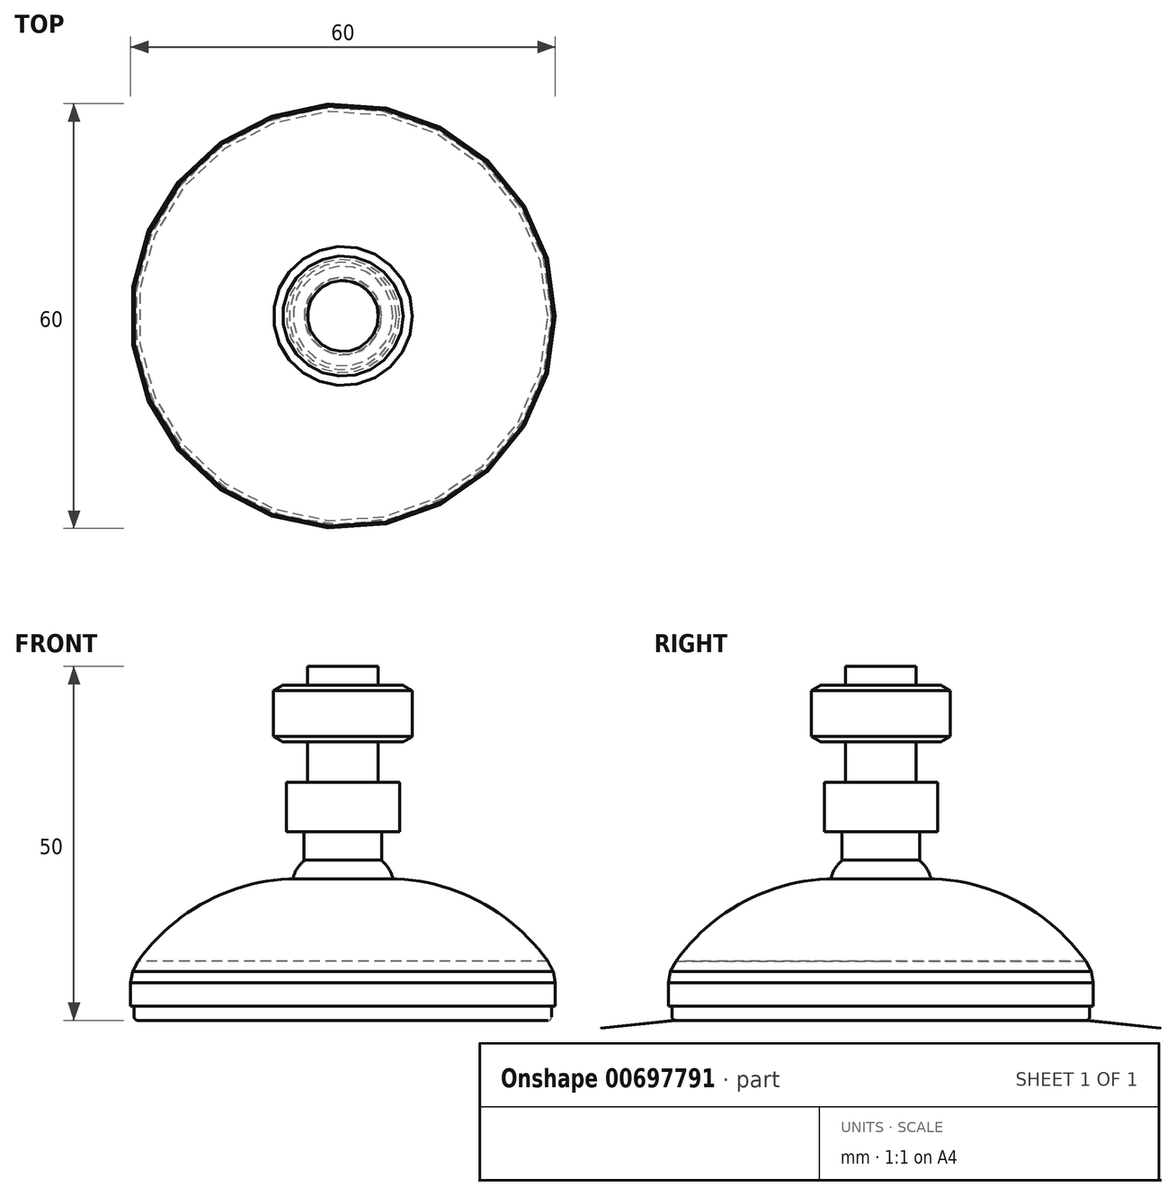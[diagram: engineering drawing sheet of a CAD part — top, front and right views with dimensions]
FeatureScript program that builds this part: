
annotation { "Feature Type Name" : "Feature", "Feature Type Description" : "" }
export const myFeature = defineFeature(function(context is Context, id is Id, definition is map)
    precondition{}
    {
        {
            var Q0;
            Q0=qCreatedBy(makeId("Front.planeOp"),FACE);
            var sketch = newSketch(context, id + "F0", { "sketchPlane" : qUnion([Q0])});
            skArc(sketch, "E0", {"start": v(-7.95, -5) * mm, "mid": v(-8.54, -3.54) * mm, "end": v(-9.6, -2.37) * mm});
            skLineSegment(sketch, "E1", {"start": v(-7, 1.63) * mm, "end": v(-7, 8.63) * mm});
            skLineSegment(sketch, "E2", {"start": v(-9.5, -2.37) * mm, "end": v(-9.5, 1.63) * mm});
            skLineSegment(sketch, "E3", {"start": v(-5.18, 21.56) * mm, "end": v(-6.5, 22.32) * mm});
            skLineSegment(sketch, "E4", {"start": v(-6.5, 14.32) * mm, "end": v(-5.18, 15.08) * mm});
            skLineSegment(sketch, "E5", {"start": v(15, -23) * mm, "end": v(15, -19.72) * mm});
            skLineSegment(sketch, "E6", {"start": v(15, -19.72) * mm, "end": v(14.73, -18.1) * mm});
            skLineSegment(sketch, "E7", {"start": v(14.73, -18.1) * mm, "end": v(13.95, -16.65) * mm});
            skArc(sketch, "E8", {"start": v(13.95, -16.65) * mm, "mid": v(4.6, -8.39) * mm, "end": v(-7.4, -5) * mm});
            skArc(sketch, "E9", {"start": v(14, -25) * mm, "mid": v(14.35, -24.85) * mm, "end": v(14.5, -24.5) * mm});
            skLineSegment(sketch, "E10", {"start": v(14.5, -24.5) * mm, "end": v(14.5, -23) * mm});
            skLineSegment(sketch, "E11", {"start": v(-9.5, 1.63) * mm, "end": v(-7, 1.63) * mm});
            skLineSegment(sketch, "E12", {"start": v(-10, 8.63) * mm, "end": v(-7, 8.63) * mm});
            skLineSegment(sketch, "E13", {"start": v(-5.18, 15.08) * mm, "end": v(-5.18, 21.56) * mm});
            skLineSegment(sketch, "E14", {"start": v(-10, 22.32) * mm, "end": v(-6.5, 22.32) * mm});
            skLineSegment(sketch, "E15", {"start": v(-10, 14.32) * mm, "end": v(-6.5, 14.32) * mm});
            skLineSegment(sketch, "E16", {"start": v(-10, 14.32) * mm, "end": v(-10, 8.63) * mm});
            skLineSegment(sketch, "E17", {"start": v(-10, 22.32) * mm, "end": v(-10, 25) * mm});
            skLineSegment(sketch, "E18", {"start": v(-10, 25) * mm, "end": v(-15, 25) * mm});
            skLineSegment(sketch, "E19", {"start": v(-15, 25) * mm, "end": v(-15, -25) * mm});
            skLineSegment(sketch, "E20", {"start": v(-15, 14.32) * mm, "end": v(-15, 14.32) * mm});
            skLineSegment(sketch, "E21", {"start": v(-15, 22.32) * mm, "end": v(-15, 22.32) * mm});
            skLineSegment(sketch, "E22", {"start": v(-15, -25) * mm, "end": v(14, -25) * mm});
            skLineSegment(sketch, "E23", {"start": v(5, -25) * mm, "end": v(-15, -25) * mm});
            skLineSegment(sketch, "E24", {"start": v(14.5, -23) * mm, "end": v(15, -23) * mm});
            skLineSegment(sketch, "E25", {"start": v(-7.95, -5) * mm, "end": v(-7.4, -5) * mm});
            skLineSegment(sketch, "E26", {"start": v(-9.6, -2.37) * mm, "end": v(-9.5, -2.37) * mm});
            skSolve(sketch);
        }
        {
            var Q0;
            Q0 = qSketchRegion(id + "F0", true);
            var Q1;
            Q1=sQuery(id+"F0.wireOp",EDGE,"E19");
            revolve(context, id + "F1", {"entities" : qUnion([Q0]), "axis" : qUnion([Q1]), "revolveType" : RevolveType.FULL});
        }
    });
